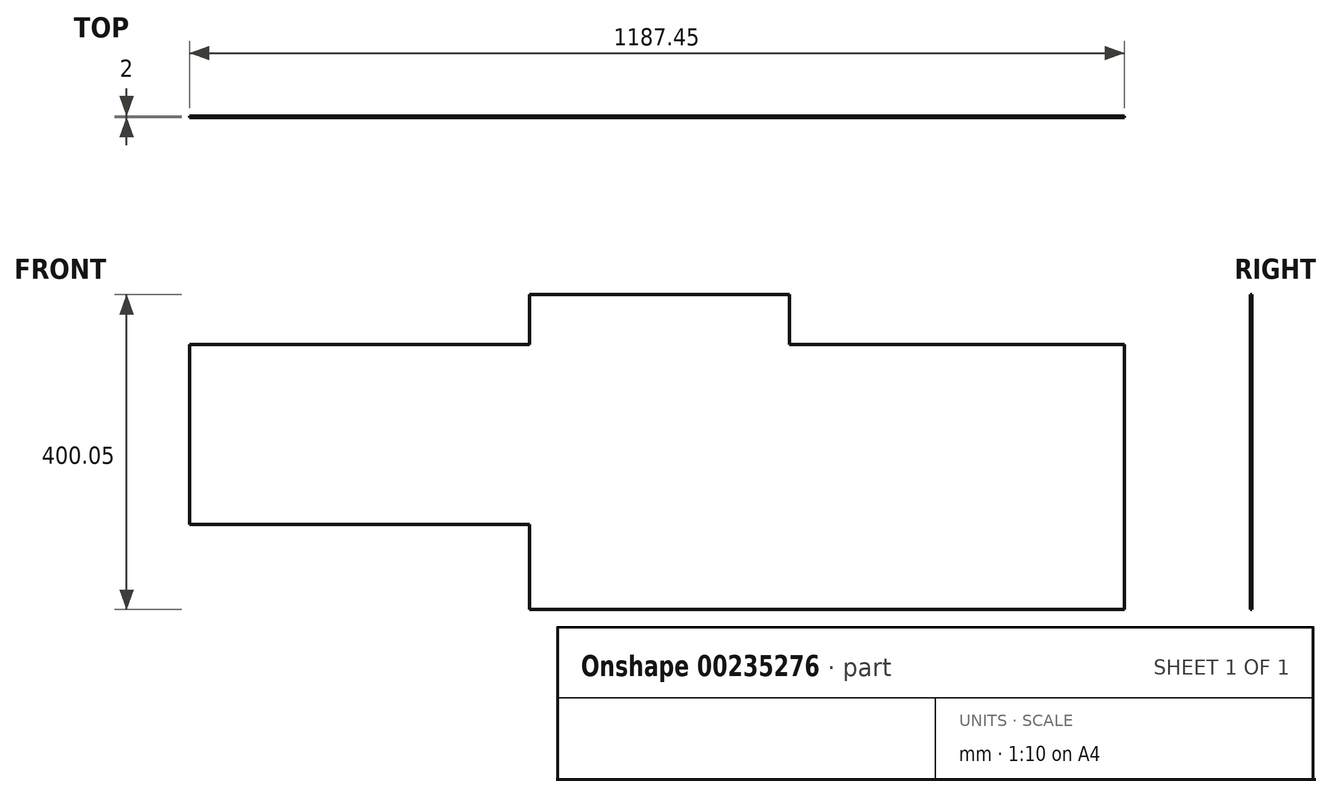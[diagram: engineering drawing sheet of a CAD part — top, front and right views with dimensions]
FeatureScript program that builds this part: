
annotation { "Feature Type Name" : "Feature", "Feature Type Description" : "" }
export const myFeature = defineFeature(function(context is Context, id is Id, definition is map)
    precondition{}
    {
        {
            var Q0;
            Q0=qCreatedBy(makeId("Front.planeOp"),FACE);
            var sketch = newSketch(context, id + "F0", { "sketchPlane" : qUnion([Q0])});
            skLineSegment(sketch, "E0", {"start": v(-47.27, 0) * mm, "end": v(-47.27, 114.3) * mm});
            skLineSegment(sketch, "E1", {"start": v(-47.27, 114.3) * mm, "end": v(384.53, 114.3) * mm});
            skLineSegment(sketch, "E2", {"start": v(384.53, 114.3) * mm, "end": v(384.53, 177.8) * mm});
            skLineSegment(sketch, "E3", {"start": v(384.53, 177.8) * mm, "end": v(714.73, 177.8) * mm});
            skLineSegment(sketch, "E4", {"start": v(714.73, 177.8) * mm, "end": v(714.73, 114.3) * mm});
            skLineSegment(sketch, "E5", {"start": v(714.73, 114.3) * mm, "end": v(1140.18, 114.3) * mm});
            skLineSegment(sketch, "E6", {"start": v(1140.18, 114.3) * mm, "end": v(1140.18, -222.25) * mm});
            skLineSegment(sketch, "E7", {"start": v(-47.27, 0) * mm, "end": v(-47.27, -114.3) * mm});
            skLineSegment(sketch, "E8", {"start": v(-47.27, -114.3) * mm, "end": v(384.53, -114.3) * mm});
            skLineSegment(sketch, "E9", {"start": v(384.53, -114.3) * mm, "end": v(384.53, -222.25) * mm});
            skLineSegment(sketch, "E10", {"start": v(384.53, -222.25) * mm, "end": v(1140.18, -222.25) * mm});
            skSolve(sketch);
        }
        {
            var Q0;
            Q0 = qSketchRegion(id + "F0", true);
            extrude(context, id + "F1", {"entities" : qUnion([Q0]), "depth" : 2 * mm});
        }
    });
